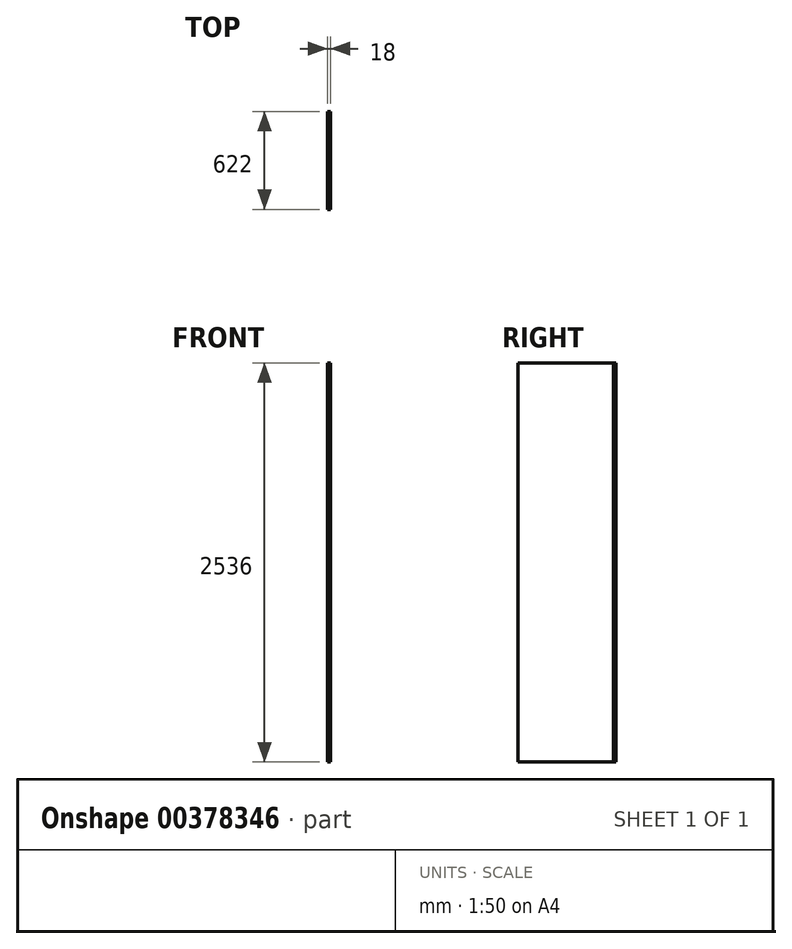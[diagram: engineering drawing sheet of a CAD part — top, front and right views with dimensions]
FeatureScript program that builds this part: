
annotation { "Feature Type Name" : "Feature", "Feature Type Description" : "" }
export const myFeature = defineFeature(function(context is Context, id is Id, definition is map)
    precondition{}
    {
        {
            var Q0;
            Q0=qCreatedBy(makeId("Right.planeOp"),FACE);
            var sketch = newSketch(context, id + "F0", { "sketchPlane" : qUnion([Q0])});
            skLineSegment(sketch, "E0.bottom", {"start": v(311, 1178.87) * mm, "end": v(-311, 1178.87) * mm});
            skLineSegment(sketch, "E0.top", {"start": v(311, -1357.13) * mm, "end": v(-311, -1357.13) * mm});
            skLineSegment(sketch, "E0.left", {"start": v(311, 1178.87) * mm, "end": v(311, -1357.13) * mm});
            skLineSegment(sketch, "E0.right", {"start": v(-311, 1178.87) * mm, "end": v(-311, -1357.13) * mm});
            skPoint(sketch, "E0.middle", {"position": v(0, -89.13) * mm});
            skSolve(sketch);
        }
        {
            var Q0;
            Q0=qSketchRegion(id+"F0",true);
            extrude(context, id + "F1", {"entities" : qUnion([Q0]), "depth" : 18 * mm});
        }
        {
            var Q0;
            Q0=makeQuery(id+"F1.opExtrude","CAP_FACE",FACE,{"disambiguationData":[OSD([sQuery(id+"F0.wireOp",EDGE,"E0.bottom"),sQuery(id+"F0.wireOp",EDGE,"E0.top"),sQuery(id+"F0.wireOp",EDGE,"E0.left"),sQuery(id+"F0.wireOp",EDGE,"E0.right")])],"isStart":false});
            var sketch = newSketch(context, id + "F2", { "sketchPlane" : qUnion([Q0])});
            skLineSegment(sketch, "E1.bottom", {"start": v(293, 1178.87) * mm, "end": v(299, 1178.87) * mm});
            skLineSegment(sketch, "E1.top", {"start": v(293, -1357.13) * mm, "end": v(299, -1357.13) * mm});
            skLineSegment(sketch, "E1.left", {"start": v(293, 1178.87) * mm, "end": v(293, -1357.13) * mm});
            skLineSegment(sketch, "E1.right", {"start": v(299, 1178.87) * mm, "end": v(299, -1357.13) * mm});
            skSolve(sketch);
        }
        {
            var Q0;
            Q0 = qSketchRegion(id + "F2", true);
            extrude(context, id + "F3", {"entities" : qUnion([Q0]), "operationType" : NewBodyOperationType.REMOVE, "oppositeDirection" : true, "depth" : 6 * mm});
        }
    });
